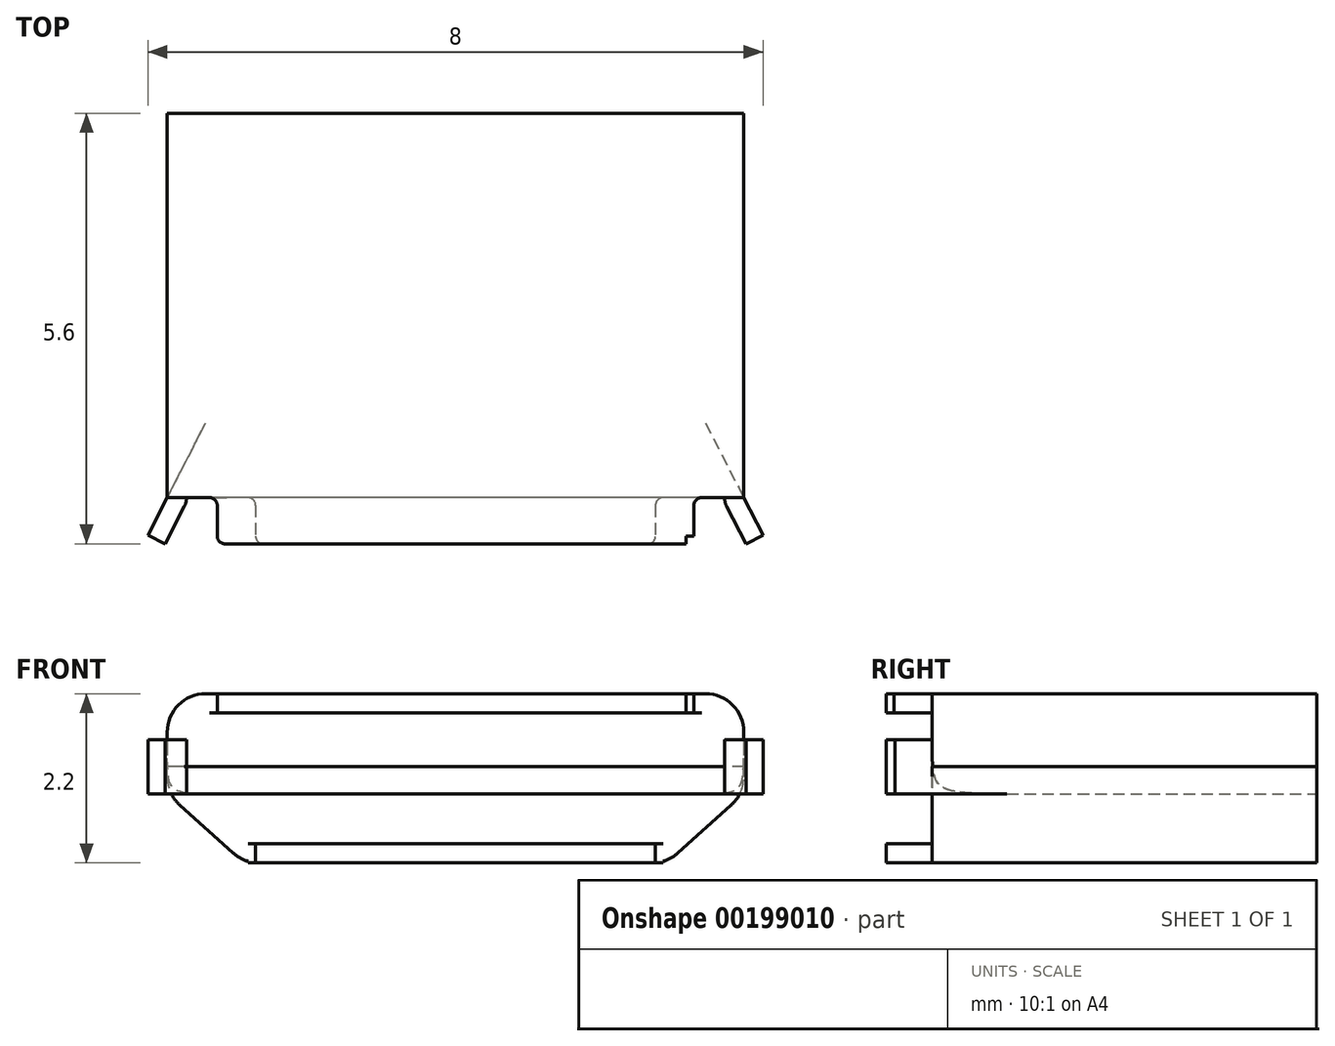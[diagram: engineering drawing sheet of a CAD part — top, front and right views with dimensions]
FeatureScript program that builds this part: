
annotation { "Feature Type Name" : "Feature", "Feature Type Description" : "" }
export const myFeature = defineFeature(function(context is Context, id is Id, definition is map)
    precondition{}
    {
        {
            var Q0;
            Q0=qCreatedBy(makeId("Top.planeOp"),FACE);
            var sketch = newSketch(context, id + "F0", { "sketchPlane" : qUnion([Q0])});
            skLineSegment(sketch, "E0.bottom", {"start": v(3.75, 2.5) * mm, "end": v(-3.75, 2.5) * mm});
            skLineSegment(sketch, "E0.top", {"start": v(3.75, -2.5) * mm, "end": v(-3.75, -2.5) * mm});
            skLineSegment(sketch, "E0.left", {"start": v(3.75, 2.5) * mm, "end": v(3.75, -2.5) * mm});
            skLineSegment(sketch, "E0.right", {"start": v(-3.75, 2.5) * mm, "end": v(-3.75, -2.5) * mm});
            skPoint(sketch, "E0.middle", {"position": v(0, 0) * mm});
            skLineSegment(sketch, "E1", {"start": v(-3.78, -3.1) * mm, "end": v(-4, -2.99) * mm});
            skLineSegment(sketch, "E2", {"start": v(-4, -2.99) * mm, "end": v(-4, -3.1) * mm});
            skLineSegment(sketch, "E3", {"start": v(-3.78, -3.1) * mm, "end": v(-3.53, -2.61) * mm});
            skLineSegment(sketch, "E4", {"start": v(-4, -2.99) * mm, "end": v(-3.75, -2.5) * mm});
            skLineSegment(sketch, "E5", {"start": v(-3.78, -3.1) * mm, "end": v(-3.75, -3.1) * mm});
            skLineSegment(sketch, "E6", {"start": v(-3.75, -3.1) * mm, "end": v(-3.75, -2.5) * mm});
            skArc(sketch, "E7", {"start": v(-3.53, -2.61) * mm, "mid": v(-3.5, -2.56) * mm, "end": v(-3.5, -2.5) * mm});
            skLineSegment(sketch, "E8", {"start": v(3.75, -2.5) * mm, "end": v(4, -2.99) * mm});
            skLineSegment(sketch, "E9", {"start": v(4, -2.99) * mm, "end": v(3.78, -3.1) * mm});
            skLineSegment(sketch, "E10", {"start": v(3.78, -3.1) * mm, "end": v(3.53, -2.61) * mm});
            skArc(sketch, "E11", {"start": v(3.53, -2.61) * mm, "mid": v(3.5, -2.56) * mm, "end": v(3.5, -2.5) * mm});
            skSolve(sketch);
        }
        {
            var Q0;
            Q0=makeQuery(id+"F0.imprint","IMPRINT",FACE,{"disambiguationData":[TD([[makeQuery(id+"F0.imprint","IMPRINT",EDGE,{"derivedFrom":sQuery(id+"F0.wireOp",EDGE,"E0.bottom")}),1.0]])]});
            var Q1;
            {var subQ3=sQuery(id+"F0.wireOp",EDGE,"E7");Q1=makeQuery(id+"F0.imprint","IMPRINT",FACE,{"disambiguationData":[TD([[makeQuery(id+"F0.imprint","IMPRINT",EDGE,{"derivedFrom":subQ3}),1.0]])]});}
            var Q2;
            {var subQ0=sQuery(id+"F0.wireOp",EDGE,"E1");Q2=makeQuery(id+"F0.imprint","IMPRINT",FACE,{"disambiguationData":[TD([[makeQuery(id+"F0.imprint","IMPRINT",EDGE,{"derivedFrom":subQ0}),-1.0]])]});}
            var Q3;
            {var subQ0=sQuery(id+"F0.wireOp",EDGE,"E8");Q3=makeQuery(id+"F0.imprint","IMPRINT",FACE,{"disambiguationData":[TD([[makeQuery(id+"F0.imprint","IMPRINT",EDGE,{"derivedFrom":subQ0}),-1.0]])]});}
            extrude(context, id + "F1", {"entities" : qUnion([Q0, Q1, Q2, Q3]), "depth" : 0.7 * mm, "symmetric" : true});
        }
        {
            var Q0;
            Q0=makeQuery(id+"F0.imprint","IMPRINT",FACE,{"disambiguationData":[TD([[makeQuery(id+"F0.imprint","IMPRINT",EDGE,{"derivedFrom":sQuery(id+"F0.wireOp",EDGE,"E0.bottom")}),1.0]])]});
            extrude(context, id + "F2", {"entities" : qUnion([Q0]), "operationType" : NewBodyOperationType.ADD, "depth" : 0.95 * mm});
        }
        {
            var Q0;
            Q0=makeQuery(id+"F0.imprint","IMPRINT",FACE,{"disambiguationData":[TD([[makeQuery(id+"F0.imprint","IMPRINT",EDGE,{"derivedFrom":sQuery(id+"F0.wireOp",EDGE,"E0.bottom")}),1.0]])]});
            extrude(context, id + "F3", {"entities" : qUnion([Q0]), "oppositeDirection" : true, "depth" : (0.9 + 0.35) * mm});
        }
        {
            var Q0;
            Q0=makeQuery(id+"F3.opExtrude","CAP_EDGE",EDGE,{"disambiguationData":[OSD([sQuery(id+"F0.wireOp",EDGE,"E0.left")])],"isStart":false});
            var Q1;
            Q1=makeQuery(id+"F3.opExtrude","CAP_EDGE",EDGE,{"disambiguationData":[OSD([sQuery(id+"F0.wireOp",EDGE,"E0.right")])],"isStart":false});
            chamfer(context, id + "F4", {"entities" : qUnion([Q0, Q1]), "chamferType" : ChamferType.TWO_OFFSETS, "width1" : 1 * mm, "oppositeDirection" : false, "width2" : 0.9 * mm, "tangentPropagation" : true});
        }
        {
            var Q0;
            {var subQ0=sQuery(id+"F0.wireOp",EDGE,"E0.left");Q0=makeQuery(id+"F4.opChamfer","BLEND_EDGE",EDGE,{"blendedFrom":[makeQuery(id+"F3.opExtrude","CAP_EDGE",EDGE,{"disambiguationData":[OSD([subQ0])],"isStart":false}),makeQuery(id+"F3.opExtrude","CAP_FACE",FACE,{"disambiguationData":[OSD([sQuery(id+"F0.wireOp",EDGE,"E0.bottom"),sQuery(id+"F0.wireOp",EDGE,"E0.top"),subQ0,sQuery(id+"F0.wireOp",EDGE,"E0.right")])],"isStart":false})],"blendedInto":[makeQuery(id+"F3.opExtrude","CAP_FACE",FACE,{"disambiguationData":[OSD([sQuery(id+"F0.wireOp",EDGE,"E0.bottom"),sQuery(id+"F0.wireOp",EDGE,"E0.top"),subQ0,sQuery(id+"F0.wireOp",EDGE,"E0.right")])],"isStart":false})]});}
            var Q1;
            {var subQ0=sQuery(id+"F0.wireOp",EDGE,"E0.right");Q1=makeQuery(id+"F4.opChamfer","BLEND_EDGE",EDGE,{"blendedFrom":[makeQuery(id+"F3.opExtrude","CAP_EDGE",EDGE,{"disambiguationData":[OSD([subQ0])],"isStart":false}),makeQuery(id+"F3.opExtrude","CAP_FACE",FACE,{"disambiguationData":[OSD([sQuery(id+"F0.wireOp",EDGE,"E0.bottom"),sQuery(id+"F0.wireOp",EDGE,"E0.top"),sQuery(id+"F0.wireOp",EDGE,"E0.left"),subQ0])],"isStart":false})],"blendedInto":[makeQuery(id+"F3.opExtrude","CAP_FACE",FACE,{"disambiguationData":[OSD([sQuery(id+"F0.wireOp",EDGE,"E0.bottom"),sQuery(id+"F0.wireOp",EDGE,"E0.top"),sQuery(id+"F0.wireOp",EDGE,"E0.left"),subQ0])],"isStart":false})]});}
            var Q2;
            {var subQ0=sQuery(id+"F0.wireOp",EDGE,"E0.left");Q2=makeQuery(id+"F4.opChamfer","BLEND_EDGE",EDGE,{"blendedFrom":[makeQuery(id+"F3.opExtrude","CAP_EDGE",EDGE,{"disambiguationData":[OSD([subQ0])],"isStart":false}),makeQuery(id+"F3.opExtrude","SWEPT_FACE",FACE,{"disambiguationData":[OSD([subQ0])]})],"blendedInto":[makeQuery(id+"F3.opExtrude","SWEPT_FACE",FACE,{"disambiguationData":[OSD([subQ0])]})]});}
            var Q3;
            {var subQ0=sQuery(id+"F0.wireOp",EDGE,"E0.right");Q3=makeQuery(id+"F4.opChamfer","BLEND_EDGE",EDGE,{"blendedFrom":[makeQuery(id+"F3.opExtrude","CAP_EDGE",EDGE,{"disambiguationData":[OSD([subQ0])],"isStart":false}),makeQuery(id+"F3.opExtrude","SWEPT_FACE",FACE,{"disambiguationData":[OSD([subQ0])]})],"blendedInto":[makeQuery(id+"F3.opExtrude","SWEPT_FACE",FACE,{"disambiguationData":[OSD([subQ0])]})]});}
            fillet(context, id + "F5", {"entities" : qUnion([Q0, Q1, Q2, Q3]), "radius" : 0.5 * mm, "tangentPropagation" : true, "allowEdgeOverflow" : false});
        }
        {
            var Q0;
            Q0=makeQuery(id+"F1.opExtrude","CAP_EDGE",EDGE,{"disambiguationData":[OSD([sQuery(id+"F0.wireOp",EDGE,"E0.right")])],"isStart":true});
            var Q1;
            Q1=makeQuery(id+"F1.opExtrude","CAP_EDGE",EDGE,{"disambiguationData":[OSD([sQuery(id+"F0.wireOp",EDGE,"E0.left")])],"isStart":true});
            fillet(context, id + "F6", {"entities" : qUnion([Q0, Q1]), "radius" : 0.5 * mm, "tangentPropagation" : true, "rho" : 0.7, "crossSection" : FilletCrossSection.CONIC, "allowEdgeOverflow" : false});
        }
        {
            var Q0;
            Q0=makeQuery(id+"F2.opExtrude","CAP_EDGE",EDGE,{"disambiguationData":[OSD([sQuery(id+"F0.wireOp",EDGE,"E0.right")])],"isStart":false});
            var Q1;
            Q1=makeQuery(id+"F2.opExtrude","CAP_EDGE",EDGE,{"disambiguationData":[OSD([sQuery(id+"F0.wireOp",EDGE,"E0.left")])],"isStart":false});
            fillet(context, id + "F7", {"entities" : qUnion([Q0, Q1]), "radius" : 0.5 * mm, "tangentPropagation" : true, "allowEdgeOverflow" : false});
        }
        {
            var Q0;
            Q0=makeQuery(id+"F2.opExtrude","CAP_FACE",FACE,{"disambiguationData":[OSD([sQuery(id+"F0.wireOp",EDGE,"E0.bottom"),sQuery(id+"F0.wireOp",EDGE,"E0.top"),sQuery(id+"F0.wireOp",EDGE,"E0.left"),sQuery(id+"F0.wireOp",EDGE,"E0.right")])],"isStart":false});
            cPlane(context, id + "F8", {"entities" : qUnion([Q0]), "cplaneType" : CPlaneType.OFFSET, "offset" : 0 * mm, "width" : 150 * mm, "height" : 150 * mm});
        }
        {
            var Q0;
            Q0=qCreatedBy(id+"F8.planeOp",FACE);
            var sketch = newSketch(context, id + "F9", { "sketchPlane" : qUnion([Q0])});
            skLineSegment(sketch, "E12", {"start": v(-3.5, -2.5) * mm, "end": v(3.5, -2.5) * mm});
            skLineSegment(sketch, "E13", {"start": v(3.5, -2.5) * mm, "end": v(3.2, -2.5) * mm});
            skArc(sketch, "E14", {"start": v(3.2, -2.5) * mm, "mid": v(3.13, -2.53) * mm, "end": v(3.1, -2.6) * mm});
            skLineSegment(sketch, "E15", {"start": v(3.1, -2.6) * mm, "end": v(3.2, -2.6) * mm});
            skLineSegment(sketch, "E16", {"start": v(3.2, -2.5) * mm, "end": v(3.2, -2.6) * mm});
            skLineSegment(sketch, "E17", {"start": v(3.1, -2.6) * mm, "end": v(3.1, -3) * mm});
            skArc(sketch, "E18", {"start": v(3.1, -3) * mm, "mid": v(3.07, -3.07) * mm, "end": v(3, -3.1) * mm});
            skLineSegment(sketch, "E19", {"start": v(3, -3) * mm, "end": v(3, -3.1) * mm});
            skLineSegment(sketch, "E20", {"start": v(3.1, -3) * mm, "end": v(3, -3) * mm});
            skLineSegment(sketch, "E21", {"start": v(-3.5, -2.5) * mm, "end": v(-3.2, -2.5) * mm});
            skArc(sketch, "E22", {"start": v(-3.2, -2.5) * mm, "mid": v(-3.13, -2.53) * mm, "end": v(-3.1, -2.6) * mm});
            skLineSegment(sketch, "E23", {"start": v(-3.2, -2.6) * mm, "end": v(-3.2, -2.5) * mm});
            skLineSegment(sketch, "E24", {"start": v(-3.2, -2.6) * mm, "end": v(-3.1, -2.6) * mm});
            skLineSegment(sketch, "E25", {"start": v(-3.1, -2.6) * mm, "end": v(-3.1, -3) * mm});
            skArc(sketch, "E26", {"start": v(-3.1, -3) * mm, "mid": v(-3.07, -3.07) * mm, "end": v(-3, -3.1) * mm});
            skLineSegment(sketch, "E27", {"start": v(-3, -3.1) * mm, "end": v(-3, -3) * mm});
            skLineSegment(sketch, "E28", {"start": v(-3.1, -3) * mm, "end": v(-3, -3) * mm});
            skLineSegment(sketch, "E29", {"start": v(-3, -3.1) * mm, "end": v(3, -3.1) * mm});
            skSolve(sketch);
        }
        {
            var Q0;
            Q0=makeQuery(id+"F9.imprint","IMPRINT",FACE,{"disambiguationData":[TD([[makeQuery(id+"F9.imprint","IMPRINT",EDGE,{"derivedFrom":sQuery(id+"F9.wireOp",EDGE,"E26")}),1.0]])]});
            var Q1;
            Q1=makeQuery(id+"F9.imprint","IMPRINT",FACE,{"disambiguationData":[TD([[makeQuery(id+"F9.imprint","IMPRINT",EDGE,{"derivedFrom":sQuery(id+"F9.wireOp",EDGE,"E12")}),-1.0]])]});
            var Q2;
            Q2=makeQuery(id+"F9.imprint","IMPRINT",FACE,{"disambiguationData":[TD([[makeQuery(id+"F9.imprint","IMPRINT",EDGE,{"derivedFrom":sQuery(id+"F9.wireOp",EDGE,"E18")}),-1.0]])]});
            extrude(context, id + "F10", {"entities" : qUnion([Q0, Q1, Q2]), "operationType" : NewBodyOperationType.ADD, "oppositeDirection" : true, "depth" : 0.25 * mm, "hasDraft" : true, "draftAngle" : 0 * degree, "draftPullDirection" : true});
        }
        {
            var Q0;
            Q0=makeQuery(id+"F3.opExtrude","CAP_FACE",FACE,{"disambiguationData":[OSD([sQuery(id+"F0.wireOp",EDGE,"E0.bottom"),sQuery(id+"F0.wireOp",EDGE,"E0.top"),sQuery(id+"F0.wireOp",EDGE,"E0.left"),sQuery(id+"F0.wireOp",EDGE,"E0.right")])],"isStart":false});
            cPlane(context, id + "F11", {"entities" : qUnion([Q0]), "cplaneType" : CPlaneType.OFFSET, "offset" : 0 * mm, "width" : 150 * mm, "height" : 150 * mm});
        }
        {
            var Q0;
            Q0=qCreatedBy(id+"F11.planeOp",FACE);
            var sketch = newSketch(context, id + "F12", { "sketchPlane" : qUnion([Q0])});
            skLineSegment(sketch, "E30", {"start": v(-2.5, 3.1) * mm, "end": v(2.5, 3.1) * mm});
            skLineSegment(sketch, "E31", {"start": v(-3.75, 2.5) * mm, "end": v(-2.7, 2.5) * mm});
            skArc(sketch, "E32", {"start": v(-2.7, 2.5) * mm, "mid": v(-2.63, 2.53) * mm, "end": v(-2.6, 2.6) * mm});
            skLineSegment(sketch, "E33", {"start": v(-2.7, 2.5) * mm, "end": v(-2.7, 2.6) * mm});
            skLineSegment(sketch, "E34", {"start": v(-2.6, 2.6) * mm, "end": v(-2.7, 2.6) * mm});
            skLineSegment(sketch, "E35", {"start": v(3.75, 2.5) * mm, "end": v(2.7, 2.5) * mm});
            skArc(sketch, "E36", {"start": v(2.7, 2.5) * mm, "mid": v(2.63, 2.53) * mm, "end": v(2.6, 2.6) * mm});
            skLineSegment(sketch, "E37", {"start": v(2.7, 2.5) * mm, "end": v(2.7, 2.6) * mm});
            skLineSegment(sketch, "E38", {"start": v(2.6, 2.6) * mm, "end": v(2.7, 2.6) * mm});
            skLineSegment(sketch, "E39", {"start": v(-2.6, 2.6) * mm, "end": v(-2.6, 3) * mm});
            skArc(sketch, "E40", {"start": v(-2.6, 3) * mm, "mid": v(-2.57, 3.07) * mm, "end": v(-2.5, 3.1) * mm});
            skLineSegment(sketch, "E41", {"start": v(-2.6, 3) * mm, "end": v(-2.5, 3) * mm});
            skLineSegment(sketch, "E42", {"start": v(-2.5, 3.1) * mm, "end": v(-2.5, 3) * mm});
            skLineSegment(sketch, "E43", {"start": v(2.6, 2.6) * mm, "end": v(2.6, 3) * mm});
            skArc(sketch, "E44", {"start": v(2.6, 3) * mm, "mid": v(2.57, 3.07) * mm, "end": v(2.5, 3.1) * mm});
            skLineSegment(sketch, "E45", {"start": v(2.5, 3.1) * mm, "end": v(2.5, 3) * mm});
            skLineSegment(sketch, "E46", {"start": v(2.6, 3) * mm, "end": v(2.5, 3) * mm});
            skLineSegment(sketch, "E47", {"start": v(2.7, 2.5) * mm, "end": v(-2.7, 2.5) * mm});
            skLineSegment(sketch, "E48", {"start": v(-2.7, 2.5) * mm, "end": v(2.7, 2.5) * mm});
            skArc(sketch, "E49", {"start": v(2.6, 2.6) * mm, "mid": v(2.63, 2.53) * mm, "end": v(2.7, 2.5) * mm});
            skLineSegment(sketch, "E50", {"start": v(2.5, 3.1) * mm, "end": v(-2.5, 3.1) * mm});
            skArc(sketch, "E51", {"start": v(-2.5, 3.1) * mm, "mid": v(-2.57, 3.07) * mm, "end": v(-2.6, 3) * mm});
            skLineSegment(sketch, "E52", {"start": v(-2.6, 3) * mm, "end": v(-2.6, 2.6) * mm});
            skSolve(sketch);
        }
        {
            var Q0;
            Q0=makeQuery(id+"F12.imprint","IMPRINT",FACE,{"disambiguationData":[TD([[makeQuery(id+"F12.imprint","IMPRINT",EDGE,{"derivedFrom":sQuery(id+"F12.wireOp",EDGE,"E41")}),-1.0]])]});
            var Q1;
            Q1=makeQuery(id+"F12.imprint","IMPRINT",FACE,{"disambiguationData":[TD([[makeQuery(id+"F12.imprint","IMPRINT",EDGE,{"derivedFrom":sQuery(id+"F12.wireOp",EDGE,"E41")}),1.0]])]});
            var Q2;
            Q2=makeQuery(id+"F12.imprint","IMPRINT",FACE,{"disambiguationData":[TD([[makeQuery(id+"F12.imprint","IMPRINT",EDGE,{"derivedFrom":sQuery(id+"F12.wireOp",EDGE,"E45")}),1.0]])]});
            extrude(context, id + "F13", {"entities" : qUnion([Q0, Q1, Q2]), "operationType" : NewBodyOperationType.ADD, "oppositeDirection" : true, "depth" : 0.25 * mm});
        }
    });
